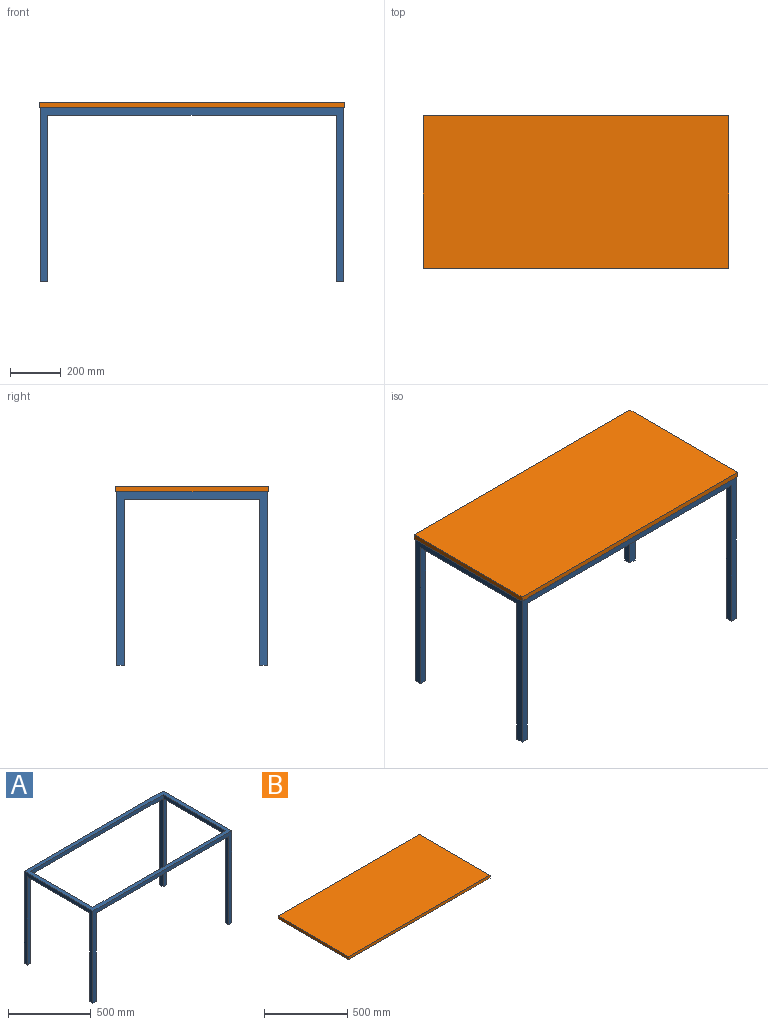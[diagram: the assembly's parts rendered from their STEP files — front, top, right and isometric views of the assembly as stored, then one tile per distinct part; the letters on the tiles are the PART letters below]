
ASSEMBLY  parts=2 mates=1
PART A: 25 faces, bbox 1190x590x682 mm
  f0: plane 534x28mm, normal (0,0,-1), area 14952mm2, adj f5,f10,f18,f21
  f1: plane 1134x28mm, normal (0,0,-1), area 31752mm2, adj f4,f7,f15,f22
  f2: plane 1134x28mm, normal (0,0,-1), area 31752mm2, adj f6,f9,f13,f19
  f3: plane 534x28mm, normal (0,0,-1), area 14952mm2, adj f8,f11,f12,f16
  f4: plane 1190x682mm, normal (0,-1,0), area 69944mm2, adj f1,f5,f11,f15,f17,f22,f23,f24
  f5: plane 682x590mm, normal (-1,0,0), area 53144mm2, adj f0,f4,f6,f18,f20,f21,f23,f24
  f6: plane 1190x682mm, normal (0,1,0), area 69944mm2, adj f2,f5,f11,f13,f14,f19,f20,f24
  f7: plane 1134x28mm, normal (0,1,0), area 31752mm2, adj f1,f8,f10,f24
  f8: plane 534x28mm, normal (-1,0,0), area 14952mm2, adj f3,f7,f9,f24
  f9: plane 1134x28mm, normal (0,-1,0), area 31752mm2, adj f2,f8,f10,f24
  f10: plane 534x28mm, normal (1,0,0), area 14952mm2, adj f0,f7,f9,f24
  f11: plane 682x590mm, normal (1,0,0), area 53144mm2, adj f3,f4,f6,f12,f14,f16,f17,f24
  f12: plane 654x28mm, normal (0,-1,0), area 18312mm2, adj f3,f11,f13,f14
  f13: plane 654x28mm, normal (-1,0,0), area 18312mm2, adj f2,f6,f12,f14
  f14: plane 28x28mm, normal (0,0,-1), area 784mm2, adj f6,f11,f12,f13
  f15: plane 654x28mm, normal (-1,0,0), area 18312mm2, adj f1,f4,f16,f17
  f16: plane 654x28mm, normal (0,1,0), area 18312mm2, adj f3,f11,f15,f17
  f17: plane 28x28mm, normal (0,0,-1), area 784mm2, adj f4,f11,f15,f16
  f18: plane 654x28mm, normal (0,-1,0), area 18312mm2, adj f0,f5,f19,f20
  f19: plane 654x28mm, normal (1,0,0), area 18312mm2, adj f2,f6,f18,f20
  f20: plane 28x28mm, normal (0,0,-1), area 784mm2, adj f5,f6,f18,f19
  f21: plane 654x28mm, normal (0,1,0), area 18312mm2, adj f0,f5,f22,f23
  f22: plane 654x28mm, normal (1,0,0), area 18312mm2, adj f1,f4,f21,f23
  f23: plane 28x28mm, normal (0,0,-1), area 784mm2, adj f4,f5,f21,f22
  f24: plane 1190x590mm, normal (0,0,1), area 96544mm2, adj f4,f5,f6,f7,f8,f9,f10,f11
PART B: 6 faces, bbox 1200x600x21 mm
  f0: plane 1200x21mm, normal (0,1,0), area 25200mm2, adj f1,f3,f4,f5
  f1: plane 600x21mm, normal (-1,0,0), area 12600mm2, adj f0,f2,f4,f5
  f2: plane 1200x21mm, normal (0,-1,0), area 25200mm2, adj f1,f3,f4,f5
  f3: plane 600x21mm, normal (1,0,0), area 12600mm2, adj f0,f2,f4,f5
  f4: plane 1200x600mm, normal (0,0,1), area 720000mm2, adj f0,f1,f2,f3
  f5: plane 1200x600mm, normal (0,0,-1), area 720000mm2, adj f0,f1,f2,f3
PLACE A at identity
PLACE B at identity fixed
MATE fastened B.f5 <-> A.f24  axis (0,0,-1) through (0,0,0)mm
